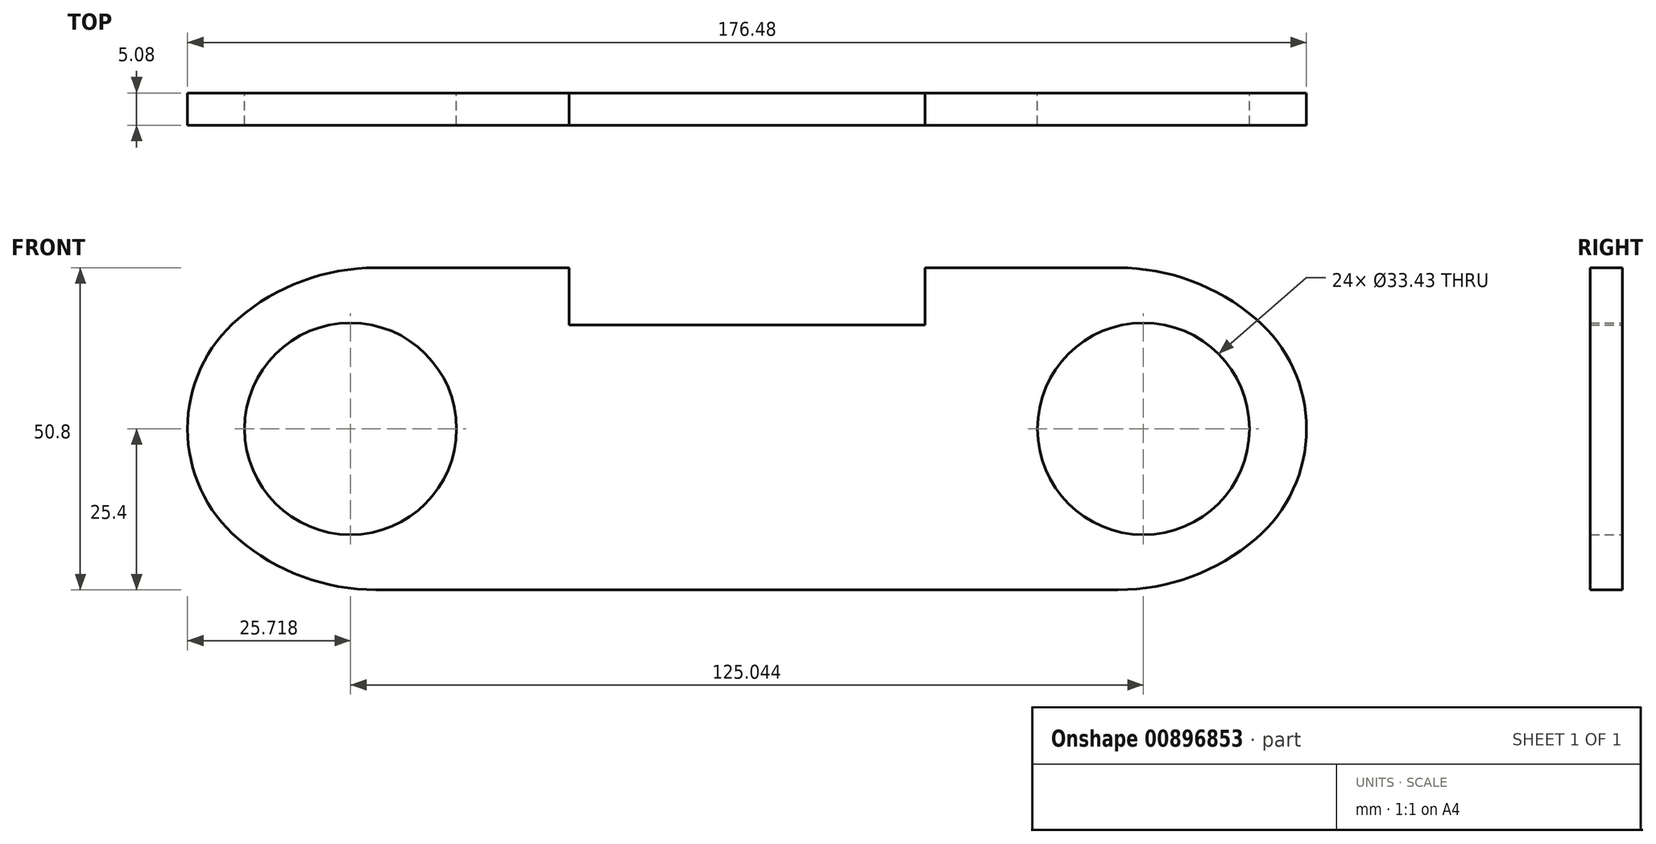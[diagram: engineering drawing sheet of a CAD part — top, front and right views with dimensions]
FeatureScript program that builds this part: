
annotation { "Feature Type Name" : "Feature", "Feature Type Description" : "" }
export const myFeature = defineFeature(function(context is Context, id is Id, definition is map)
    precondition{}
    {
        {
            var Q0;
            Q0=qCreatedBy(makeId("Front.planeOp"),FACE);
            var sketch = newSketch(context, id + "F0", { "sketchPlane" : qUnion([Q0])});
            skLineSegment(sketch, "E0.bottom", {"start": v(91.94, -25.4) * mm, "end": v(-91.94, -25.4) * mm});
            skLineSegment(sketch, "E0.top", {"start": v(91.94, 25.4) * mm, "end": v(-91.94, 25.4) * mm});
            skLineSegment(sketch, "E0.left", {"start": v(91.94, -25.4) * mm, "end": v(91.94, 25.4) * mm});
            skLineSegment(sketch, "E0.right", {"start": v(-91.94, -25.4) * mm, "end": v(-91.94, 25.4) * mm});
            skPoint(sketch, "E0.middle", {"position": v(0, 0) * mm});
            skCircle(sketch, "E1", {"center": v(-62.52, 0) * mm, "radius": 16.71 * mm});
            skCircle(sketch, "E2", {"center": v(62.52, 0) * mm, "radius": 16.71 * mm});
            skLineSegment(sketch, "E3.bottom", {"start": v(28.07, 16.4) * mm, "end": v(-28.07, 16.4) * mm});
            skLineSegment(sketch, "E3.top", {"start": v(28.07, 34.4) * mm, "end": v(-28.07, 34.4) * mm});
            skLineSegment(sketch, "E3.left", {"start": v(28.07, 16.4) * mm, "end": v(28.07, 34.4) * mm});
            skLineSegment(sketch, "E3.right", {"start": v(-28.07, 16.4) * mm, "end": v(-28.07, 34.4) * mm});
            skPoint(sketch, "E3.middle", {"position": v(0, 25.4) * mm});
            skSolve(sketch);
        }
        {
            var Q0;
            Q0=makeQuery(id+"F0.imprint","IMPRINT",FACE,{"disambiguationData":[TD([[makeQuery(id+"F0.imprint","IMPRINT",EDGE,{"derivedFrom":sQuery(id+"F0.wireOp",EDGE,"E0.bottom")}),-1.0]])]});
            extrude(context, id + "F1", {"entities" : qUnion([Q0]), "depth" : 5.08 * mm, "offsetDistance" : 25.4 * mm});
        }
        {
            var Q0;
            Q0=makeQuery(id+"F1.opExtrude","SWEPT_EDGE",EDGE,{"disambiguationData":[OSD([sQuery(id+"F0.wireOp",EDGE,"E0.top"),sQuery(id+"F0.wireOp",EDGE,"E0.left")])]});
            var Q1;
            Q1=makeQuery(id+"F1.opExtrude","SWEPT_EDGE",EDGE,{"disambiguationData":[OSD([sQuery(id+"F0.wireOp",EDGE,"E0.bottom"),sQuery(id+"F0.wireOp",EDGE,"E0.left")])]});
            var Q2;
            Q2=makeQuery(id+"F1.opExtrude","SWEPT_EDGE",EDGE,{"disambiguationData":[OSD([sQuery(id+"F0.wireOp",EDGE,"E0.top"),sQuery(id+"F0.wireOp",EDGE,"E0.right")])]});
            var Q3;
            Q3=makeQuery(id+"F1.opExtrude","SWEPT_EDGE",EDGE,{"disambiguationData":[OSD([sQuery(id+"F0.wireOp",EDGE,"E0.bottom"),sQuery(id+"F0.wireOp",EDGE,"E0.right")])]});
            fillet(context, id + "F2", {"entities" : qUnion([Q0, Q1, Q2, Q3]), "radius" : 33.43 * mm, "tangentPropagation" : true, "allowEdgeOverflow" : false});
        }
        {
            var Q0;
            {var subQ0=sQuery(id+"F0.wireOp",EDGE,"E0.right");Q0=makeQuery(id+"F2.opFillet","BLEND_EDGE",EDGE,{"blendedFrom":[makeQuery(id+"F1.opExtrude","SWEPT_EDGE",EDGE,{"disambiguationData":[OSD([sQuery(id+"F0.wireOp",EDGE,"E0.bottom"),subQ0])]}),makeQuery(id+"F1.opExtrude","SWEPT_EDGE",EDGE,{"disambiguationData":[OSD([sQuery(id+"F0.wireOp",EDGE,"E0.top"),subQ0])]})],"blendedInto":[]});}
            fillet(context, id + "F3", {"entities" : qUnion([Q0]), "radius" : 22.86 * mm, "tangentPropagation" : true, "allowEdgeOverflow" : false});
        }
        {
            var Q0;
            {var subQ0=sQuery(id+"F0.wireOp",EDGE,"E0.left");Q0=makeQuery(id+"F2.opFillet","BLEND_EDGE",EDGE,{"blendedFrom":[makeQuery(id+"F1.opExtrude","SWEPT_EDGE",EDGE,{"disambiguationData":[OSD([sQuery(id+"F0.wireOp",EDGE,"E0.bottom"),subQ0])]}),makeQuery(id+"F1.opExtrude","SWEPT_EDGE",EDGE,{"disambiguationData":[OSD([sQuery(id+"F0.wireOp",EDGE,"E0.top"),subQ0])]})],"blendedInto":[]});}
            fillet(context, id + "F4", {"entities" : qUnion([Q0]), "radius" : 22.86 * mm, "tangentPropagation" : true, "allowEdgeOverflow" : false});
        }
    });
